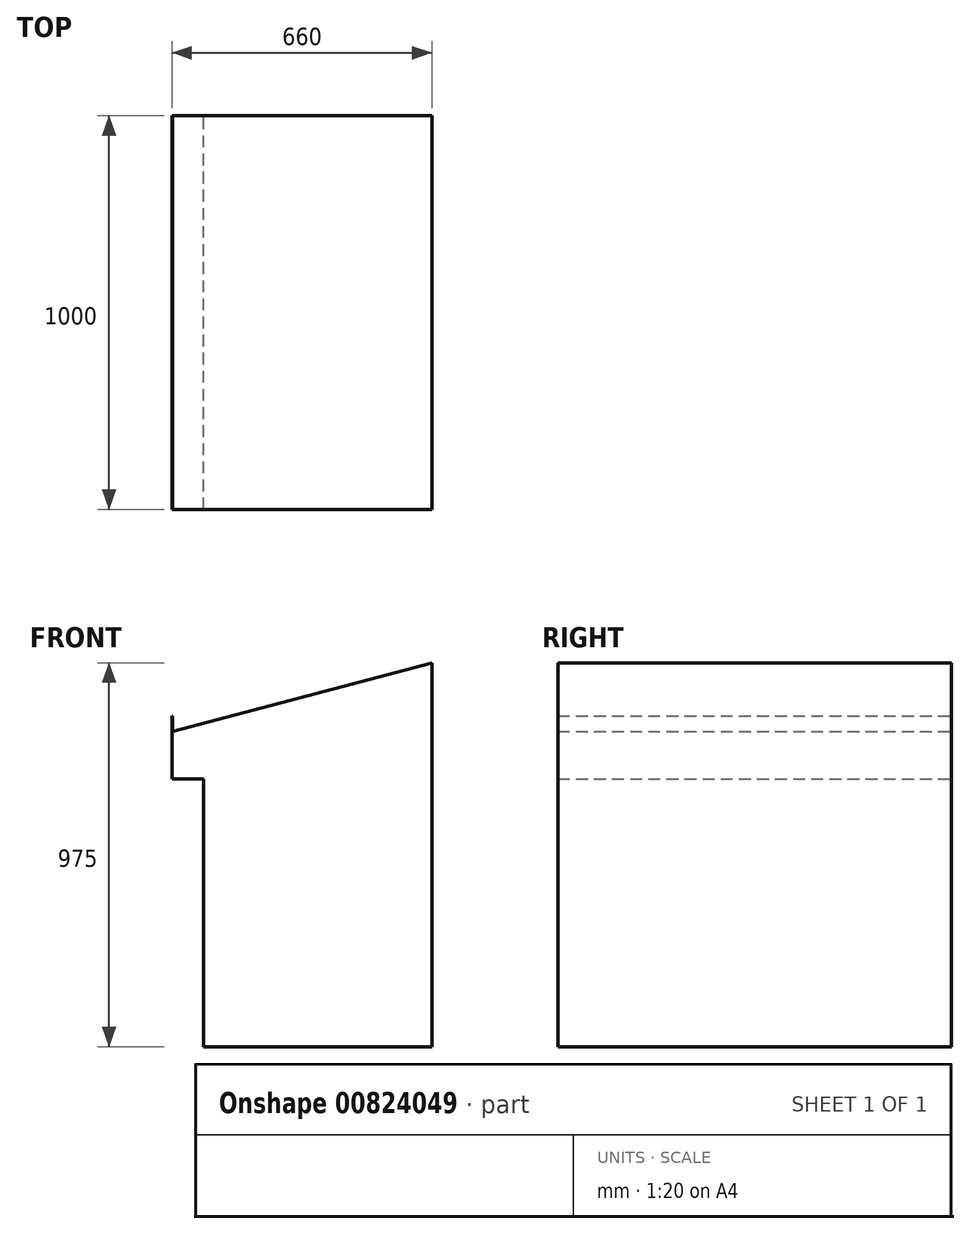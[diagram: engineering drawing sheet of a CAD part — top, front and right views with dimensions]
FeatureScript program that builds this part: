
annotation { "Feature Type Name" : "Feature", "Feature Type Description" : "" }
export const myFeature = defineFeature(function(context is Context, id is Id, definition is map)
    precondition{}
    {
        {
            var Q0;
            Q0=qCreatedBy(makeId("Front.planeOp"),FACE);
            var sketch = newSketch(context, id + "F0", { "sketchPlane" : qUnion([Q0])});
            skLineSegment(sketch, "E0", {"start": v(0, 0) * mm, "end": v(0, 800) * mm});
            skLineSegment(sketch, "E1", {"start": v(0, 800) * mm, "end": v(660, 975) * mm});
            skLineSegment(sketch, "E2", {"start": v(660, 975) * mm, "end": v(660, 0) * mm});
            skLineSegment(sketch, "E3", {"start": v(660, 0) * mm, "end": v(0, 0) * mm});
            skSolve(sketch);
        }
        {
            var Q0;
            Q0 = qSketchRegion(id + "F0", true);
            extrude(context, id + "F1", {"entities" : qUnion([Q0]), "depth" : 1000 * mm, "offsetDistance" : 25 * mm});
        }
        {
            var Q0;
            Q0=qCreatedBy(makeId("Front.planeOp"),FACE);
            var sketch = newSketch(context, id + "F2", { "sketchPlane" : qUnion([Q0])});
            skLineSegment(sketch, "E4.0", {"start": v(0, 800) * mm, "end": v(660, 975) * mm, "construction": true});
            skLineSegment(sketch, "E5.0", {"start": v(0, 0) * mm, "end": v(0, 800) * mm, "construction": true});
            skLineSegment(sketch, "E6", {"start": v(0, 800) * mm, "end": v(0, 840) * mm});
            skLineSegment(sketch, "E7", {"start": v(0, 840) * mm, "end": v(1.5, 840) * mm});
            skLineSegment(sketch, "E8", {"start": v(1.5, 840) * mm, "end": v(1.5, 800.4) * mm});
            skLineSegment(sketch, "E9", {"start": v(1.5, 800.4) * mm, "end": v(0, 800) * mm});
            skSolve(sketch);
        }
        {
            var Q0;
            Q0 = qSketchRegion(id + "F2", true);
            var Q1;
            Q1=makeQuery(id+"F1.opExtrude","CAP_FACE",FACE,{"disambiguationData":[OSD([sQuery(id+"F0.wireOp",EDGE,"E0"),sQuery(id+"F0.wireOp",EDGE,"E1"),sQuery(id+"F0.wireOp",EDGE,"E2"),sQuery(id+"F0.wireOp",EDGE,"E3")])],"isStart":false});
            extrude(context, id + "F3", {"entities" : qUnion([Q0]), "operationType" : NewBodyOperationType.ADD, "endBound" : BoundingType.UP_TO_SURFACE, "depth" : 25 * mm, "endBoundEntityFace" : qUnion([Q1]), "offsetDistance" : 25 * mm});
        }
        {
            var Q0;
            Q0=makeQuery(id+"F3.boolean.opBoolean","MERGE",FACE,{"derivedFrom":[makeQuery(id+"F1.opExtrude","CAP_FACE",FACE,{"disambiguationData":[OSD([sQuery(id+"F0.wireOp",EDGE,"E0"),sQuery(id+"F0.wireOp",EDGE,"E1"),sQuery(id+"F0.wireOp",EDGE,"E2"),sQuery(id+"F0.wireOp",EDGE,"E3")])],"isStart":true}),makeQuery(id+"F3.opExtrude","CAP_FACE",FACE,{"disambiguationData":[OSD([sQuery(id+"F2.wireOp",EDGE,"E6"),sQuery(id+"F2.wireOp",EDGE,"E7"),sQuery(id+"F2.wireOp",EDGE,"E8"),sQuery(id+"F2.wireOp",EDGE,"E9")])],"isStart":true})]});
            var sketch = newSketch(context, id + "F4", { "sketchPlane" : qUnion([Q0])});
            skLineSegment(sketch, "E10.0", {"start": v(-1.5, 800.4) * mm, "end": v(-660, 975) * mm, "construction": true});
            skLineSegment(sketch, "E11.0", {"start": v(0, 0) * mm, "end": v(0, 840) * mm, "construction": true});
            skLineSegment(sketch, "E12", {"start": v(0, 680.4) * mm, "end": v(-80, 680.4) * mm});
            skLineSegment(sketch, "E13", {"start": v(-80, 680.4) * mm, "end": v(-80, 0) * mm});
            skLineSegment(sketch, "E14", {"start": v(-80, 0) * mm, "end": v(0, 0) * mm});
            skSolve(sketch);
        }
        {
            var Q0;
            {var subQ0=sQuery(id+"F4.wireOp",EDGE,"E12");Q0=makeQuery(id+"F4.imprint","IMPRINT",FACE,{"disambiguationData":[TD([[makeQuery(id+"F4.imprint","IMPRINT",EDGE,{"derivedFrom":subQ0}),1.0]])]});}
            extrude(context, id + "F5", {"entities" : qUnion([Q0]), "operationType" : NewBodyOperationType.REMOVE, "endBound" : BoundingType.UP_TO_NEXT, "oppositeDirection" : true, "depth" : 25 * mm, "offsetDistance" : 25 * mm});
        }
    });
